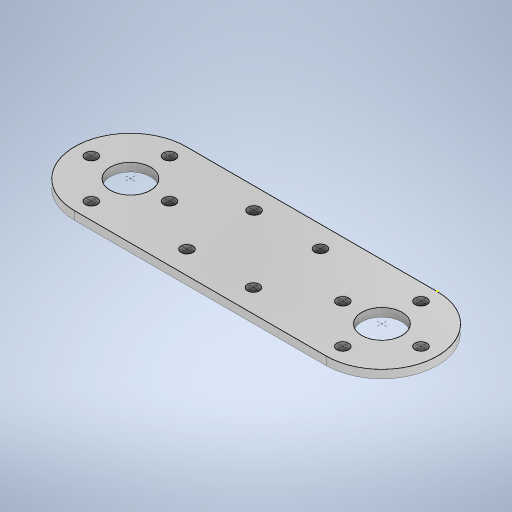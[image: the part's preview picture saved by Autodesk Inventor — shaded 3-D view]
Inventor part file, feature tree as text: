
AUTODESK INVENTOR PART (.ipt)
format: ipt  version: 2024.2 (Build 282272000, 272)  size: 265,216 bytes
history: native  units: in
note: dims shown in document units (in); Inventor stores cm internally (conversion verified against a paired STEP export)
features: sketch x1, extrude x1
ambient origin geometry x8: Origin, YZ Plane, XZ Plane, XY Plane, X Axis, Y Axis, Z Axis, Center Point
bodies: Solid1 (feature_tree)
feature tree (2):
  sketch  "Sketch1"  dims[d0=0.0591in d1=0.0in]
  extrude  "Extrusion1"  [1 undecoded]
note: 1 required parameter value undecoded (feature->parameter linkage not recoverable at this tier; creation-order binding heuristic only, values carry confidence <= 0.55)
